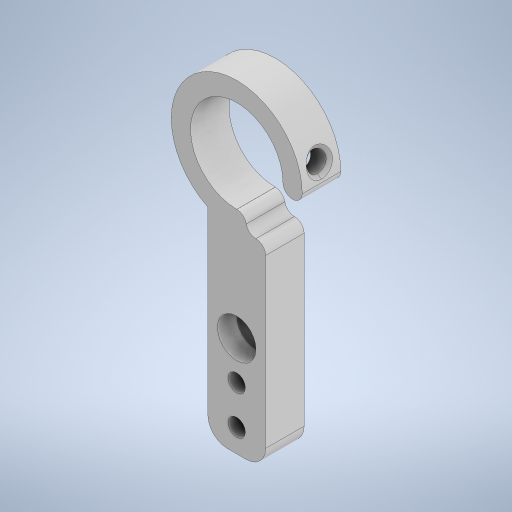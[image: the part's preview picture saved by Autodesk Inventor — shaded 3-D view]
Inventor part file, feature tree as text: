
AUTODESK INVENTOR PART (.ipt)
format: ipt  version: 2023 (Build 270158000, 158)  size: 333,312 bytes
history: native  units: mm
features: sketch x5, extrude x4, fillet x2, other x1, revolve x1, chamfer x1
ambient origin geometry x8: Origin, YZ Plane, XZ Plane, XY Plane, X Axis, Y Axis, Z Axis, Center Point
bodies: Body1 (feature_tree)
feature tree (14):
  other  "솔리드1"
  extrude  "돌출1"  Depth=15.0mm
  fillet  "모깎기1"  Radius=55.0mm
  revolve  "회전1"
  chamfer  "모따기1"  Distance=24.0mm
  extrude  "돌출2"  Depth=34.0mm
  fillet  "모깎기2"  Radius=10.0mm
  extrude  "돌출4"  Depth=2.5mm
  extrude  "돌출5"  Depth=1.745329mm
  sketch  "스케치1"
  sketch  "스케치2"
  sketch  "스케치3"
  sketch  "스케치5"
  sketch  "스케치6"
